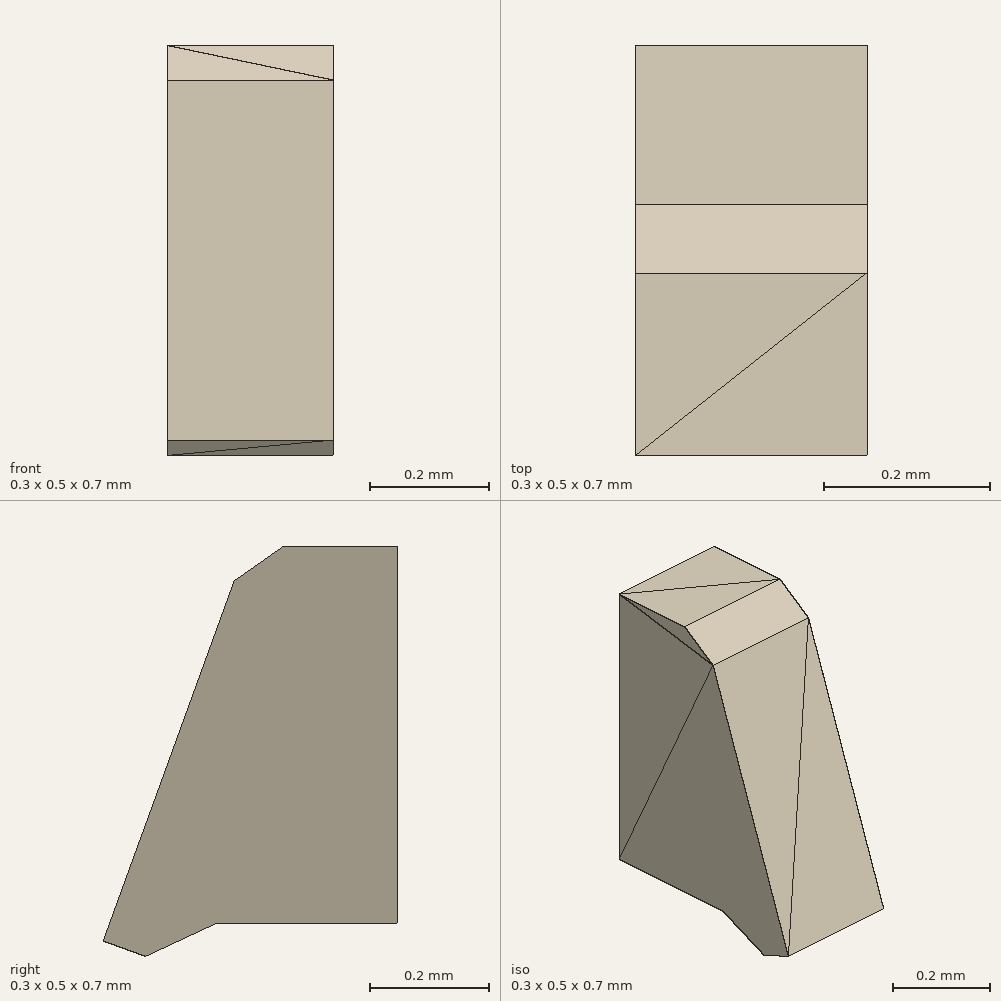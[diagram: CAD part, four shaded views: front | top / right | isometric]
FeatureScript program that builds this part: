
annotation { "Feature Type Name" : "Feature", "Feature Type Description" : "" }
export const myFeature = defineFeature(function(context is Context, id is Id, definition is map)
    precondition{}
    {
        {
            var Q0;
            Q0=qCreatedBy(makeId("Right.planeOp"),FACE);
            var sketch = newSketch(context, id + "F0", { "sketchPlane" : qUnion([Q0])});
            skLineSegment(sketch, "E0", {"start": v(0, 0.32) * mm, "end": v(0, -0.32) * mm});
            skLineSegment(sketch, "E1", {"start": v(-0.08, 0.57) * mm, "end": v(-0.08, -0.71) * mm, "construction": true});
            skLineSegment(sketch, "E2", {"start": v(0, 0.32) * mm, "end": v(-0.25, 0.32) * mm});
            skLineSegment(sketch, "E3", {"start": v(-0.5, -0.35) * mm, "end": v(-0.42, -0.37) * mm});
            skLineSegment(sketch, "E4", {"start": v(-0.3, -0.32) * mm, "end": v(0, -0.32) * mm});
            skLineSegment(sketch, "E5", {"start": v(-0.25, 0.32) * mm, "end": v(-0.5, -0.35) * mm});
            skLineSegment(sketch, "E6", {"start": v(-0.42, -0.37) * mm, "end": v(-0.3, -0.32) * mm});
            skLineSegment(sketch, "E7", {"start": v(-0.28, 0.26) * mm, "end": v(-0.2, 0.32) * mm});
            skLineSegment(sketch, "E8", {"start": v(-0.25, 0.32) * mm, "end": v(-0.23, 0.29) * mm, "construction": true});
            skSolve(sketch);
        }
        {
            var Q0;
            Q0=makeQuery(id+"F0.imprint","IMPRINT",FACE,{"disambiguationData":[TD([[makeQuery(id+"F0.imprint","IMPRINT",EDGE,{"derivedFrom":sQuery(id+"F0.wireOp",EDGE,"E0")}),-1.0]])]});
            extrude(context, id + "F1", {"entities" : qUnion([Q0]), "depth" : 0.28 * mm, "symmetric" : true});
        }
        {
            var Q0;
            Q0=makeQuery(id+"F1.opExtrude","SWEPT_BODY",BODY,{"disambiguationData":[OSD([sQuery(id+"F0.wireOp",EDGE,"E0"),sQuery(id+"F0.wireOp",EDGE,"E2"),sQuery(id+"F0.wireOp",EDGE,"E3"),sQuery(id+"F0.wireOp",EDGE,"E4"),sQuery(id+"F0.wireOp",EDGE,"E5"),sQuery(id+"F0.wireOp",EDGE,"E6"),sQuery(id+"F0.wireOp",EDGE,"E7")])]});
            transform(context, id + "F2", {"entities" : qUnion([Q0]), "transformType" : TransformType.COPY});
        }
    });
